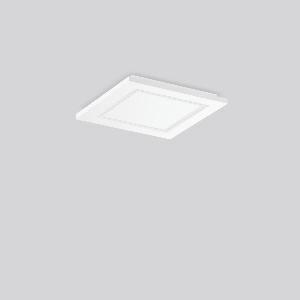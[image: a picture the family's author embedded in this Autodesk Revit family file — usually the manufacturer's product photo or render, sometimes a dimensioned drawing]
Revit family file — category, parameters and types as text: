
# Revit family: hemis_square_312188_002_3_a612
name_source: partatom
category: Lighting Fixtures
units: mm (PartAtom-declared; Revit-internal decimal feet)

## family parameters
Cut with Voids When Loaded = No
Host = Face
Light Source = No
Part Type = Normal
Room Calculation Point = No
Round Connector Dimension = Use Diameter
Shared = No

## types (1)
- MultiLumen 1 (1 x LED Modul 840, 2300 lm, 4000)
    Apparent Load = 16 VA
    CIE Flux Codes = 87 99 100 100 100
    Color Rendering = 80
    Color Temperature = 4000
    Default Elevation = 1800 mm
    Description = Series: HEMIS square
Glare-free LED ceiling luminaire with optical lens system. Base: metal, powder-coated, with bayonet fixing. Housing: plastic (polycarbonate). Housing and diffuser are screwed together. Diffuser with optic lenses. Big terminal block; ideal for through-wiring. Sealing strip on the back of the luminaire connects seamlessly with the ceiling. Easy installation with Plug+Play plug connection. Thanks to RUG < 22 ideal for corridors, stairways, shops, schools, meeting rooms, rest areas. 
Colour: white
Length: 300 mm
Width: 300 mm
Height: 33 mm
Lamp: LED
Socket: without socket
Colour temperature: 4000K
Colour rendering index (CRI): 80
System power: 16 W
Rated luminous flux: 2300 lm
Luminous efficiency: 144 lm/W
System power 2: 10 W
Rated luminous flux 2: 1450 lm
Luminous efficiency 2: 145 lm/W
Control gear: Regulated power supply
Protection class: I
Type of protection: IP 40
    Height = 33 mm
    Lamp = 1 x LED Modul 840
    Lamp Light Flux = 2300 lm
    Lamp count = 1
    Length = 300 mm
    Lifetime = 50000 h
    Luminous efficacy = 144 lm/W
    Manufacturer = RZB
    ModVariant = No
    Model = 312188.002.3
    Mounting Place = Ceiling
    Mounting Type = Surface mounted
    Number of Poles = 1
    OnlyDefault = Yes
    Power Factor = 1
    Product Name = HEMIS square
    Product group = Surface mounted modular luminaires
    ProductGroupID = 306
    Protection Class = Protection class I
    Protection Degree = Degree of protection
    RLX_Detail_Level = 1
    RLX_Emergency_Light_Flux = 0 lm
    RLX_Emergency_Type = 0
    RLX_Emergency_Type_DB = No
    RlxData = <blob elided: 13101 chars, md5=bc3f655a>
    Socket = socket
    Standby Power = 0 W
    System Light Flux = 2300 lm
    System Power = 16 W
    Type Comments = MultiLumen 1
    Type Image = 312188.002.jpg
    URL = http://relux.com
    VarID = multilumen_1
    Voltage = 0 V
    Weight = 0.00 kg
    Width = 300 mm

## geometry (parser evidence)
native form markers: Sweep x9
no freeform markers — native parametric forms only
